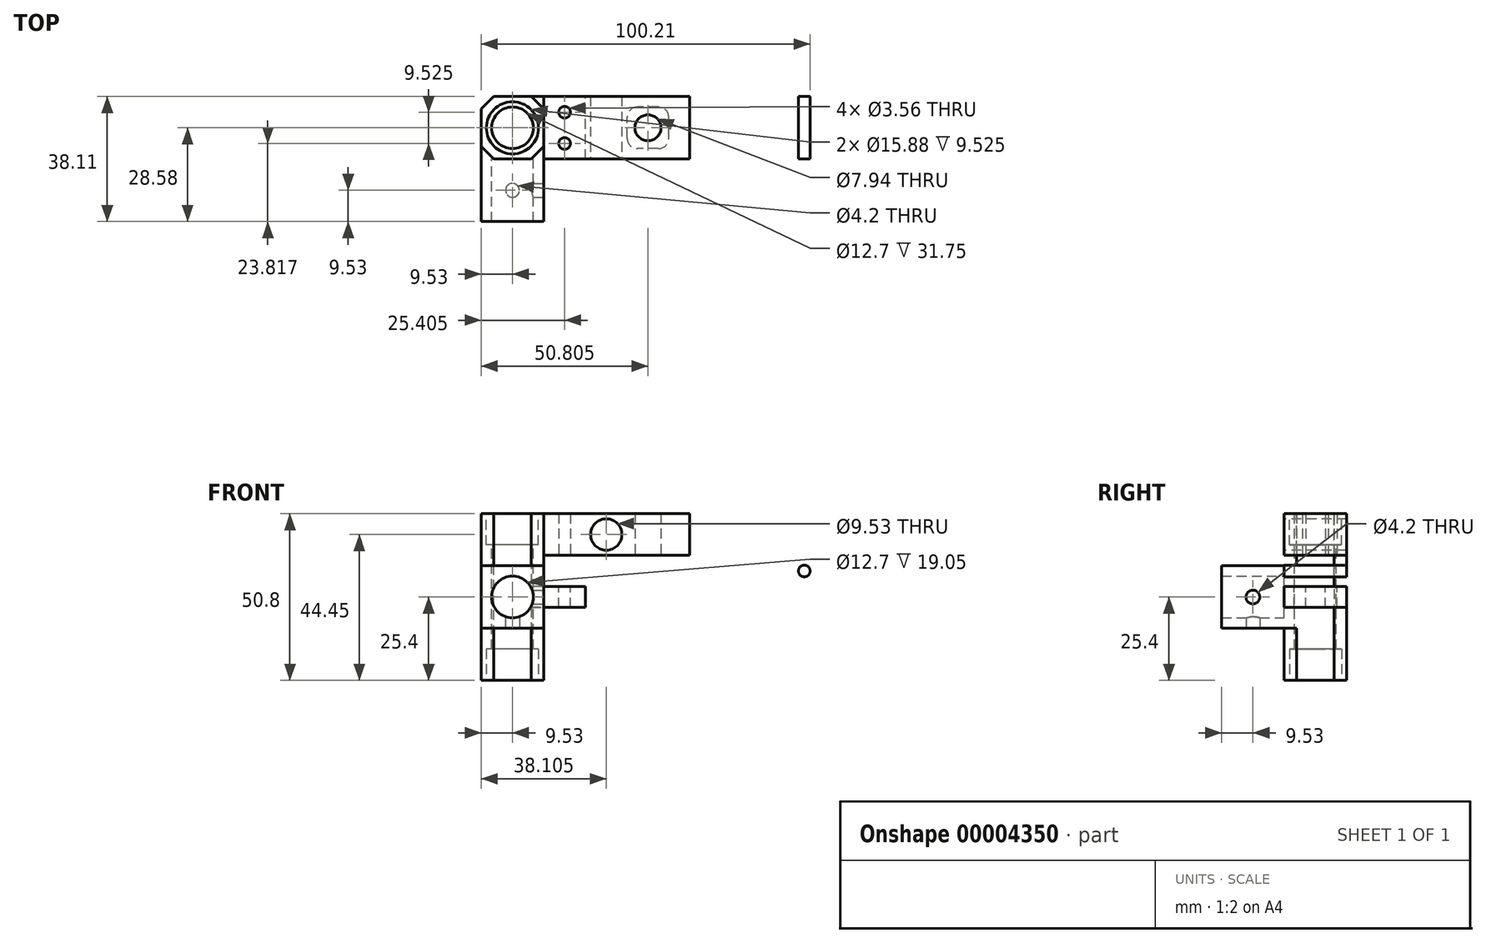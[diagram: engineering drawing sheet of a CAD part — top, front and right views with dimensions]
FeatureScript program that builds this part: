
annotation { "Feature Type Name" : "Feature", "Feature Type Description" : "" }
export const myFeature = defineFeature(function(context is Context, id is Id, definition is map)
    precondition{}
    {
        {
            var Q0;
            Q0=qCreatedBy(makeId("Front.planeOp"),FACE);
            var sketch = newSketch(context, id + "F0", { "sketchPlane" : qUnion([Q0])});
            skLineSegment(sketch, "E0.bottom", {"start": v(-9.52, -25.4) * mm, "end": v(9.53, -25.4) * mm});
            skLineSegment(sketch, "E0.top", {"start": v(-9.53, 0) * mm, "end": v(9.53, 0) * mm});
            skLineSegment(sketch, "E0.left", {"start": v(-9.52, -25.4) * mm, "end": v(-9.53, 0) * mm});
            skLineSegment(sketch, "E0.right", {"start": v(9.53, -25.4) * mm, "end": v(9.53, 0) * mm});
            skSolve(sketch);
        }
        {
            var Q0;
            Q0=makeQuery(id+"F0.imprint","IMPRINT",FACE,{"disambiguationData":[TD([[makeQuery(id+"F0.imprint","IMPRINT",EDGE,{"derivedFrom":sQuery(id+"F0.wireOp",EDGE,"E0.bottom")}),1.0]])]});
            extrude(context, id + "F1", {"entities" : qUnion([Q0]), "depth" : 19.05 * mm, "symmetric" : true});
        }
        {
            var Q0;
            Q0=makeQuery(id+"F1.opExtrude","SWEPT_FACE",FACE,{"disambiguationData":[OSD([sQuery(id+"F0.wireOp",EDGE,"E0.top")])]});
            var sketch = newSketch(context, id + "F2", { "sketchPlane" : qUnion([Q0])});
            skCircle(sketch, "E1", {"center": v(0, 0) * mm, "radius": 6.35 * mm});
            skCircle(sketch, "E2", {"center": v(0, 0) * mm, "radius": 7.94 * mm});
            skSolve(sketch);
        }
        {
            var Q0;
            Q0=makeQuery(id+"F2.imprint","IMPRINT",FACE,{"disambiguationData":[TD([[makeQuery(id+"F2.imprint","IMPRINT",EDGE,{"derivedFrom":sQuery(id+"F2.wireOp",EDGE,"E1")}),1.0]])]});
            extrude(context, id + "F3", {"entities" : qUnion([Q0]), "operationType" : NewBodyOperationType.REMOVE, "endBound" : BoundingType.UP_TO_NEXT, "oppositeDirection" : true, "depth" : 25.4 * mm});
        }
        {
            var Q0;
            Q0=makeQuery(id+"F2.imprint","IMPRINT",FACE,{"disambiguationData":[TD([[makeQuery(id+"F2.imprint","IMPRINT",EDGE,{"derivedFrom":sQuery(id+"F2.wireOp",EDGE,"E1")}),-1.0]])]});
            extrude(context, id + "F4", {"entities" : qUnion([Q0]), "operationType" : NewBodyOperationType.REMOVE, "oppositeDirection" : true, "depth" : 9.52 * mm});
        }
        {
            var Q0;
            Q0=makeQuery(id+"F1.opExtrude","SWEPT_BODY",BODY,{"disambiguationData":[OSD([sQuery(id+"F0.wireOp",EDGE,"E0.bottom"),sQuery(id+"F0.wireOp",EDGE,"E0.top"),sQuery(id+"F0.wireOp",EDGE,"E0.left"),sQuery(id+"F0.wireOp",EDGE,"E0.right")])]});
            var Q1;
            Q1=makeQuery(id+"F1.opExtrude","SWEPT_FACE",FACE,{"disambiguationData":[OSD([sQuery(id+"F0.wireOp",EDGE,"E0.bottom")])]});
            mirror(context, id + "F5", {"entities" : qUnion([Q0]), "mirrorPlane" : qUnion([Q1])});
        }
        {
            var Q0;
            Q0=makeQuery(id+"F1.opExtrude","SWEPT_BODY",BODY,{"disambiguationData":[OSD([sQuery(id+"F0.wireOp",EDGE,"E0.bottom"),sQuery(id+"F0.wireOp",EDGE,"E0.top"),sQuery(id+"F0.wireOp",EDGE,"E0.left"),sQuery(id+"F0.wireOp",EDGE,"E0.right")])]});
            var Q1;
            Q1=makeQuery(id+"F5.opPattern","COPY",BODY,{"derivedFrom":makeQuery(id+"F1.opExtrude","SWEPT_BODY",BODY,{"disambiguationData":[OSD([sQuery(id+"F0.wireOp",EDGE,"E0.bottom"),sQuery(id+"F0.wireOp",EDGE,"E0.top"),sQuery(id+"F0.wireOp",EDGE,"E0.left"),sQuery(id+"F0.wireOp",EDGE,"E0.right")])]}),"instanceName":"1"});
            booleanBodies(context, id + "F6", {"operationType" : BooleanOperationType.UNION, "tools" : qUnion([Q0, Q1])});
        }
        {
            var Q0;
            {var subQ0=makeQuery(id+"F1.opExtrude","CAP_FACE",FACE,{"disambiguationData":[OSD([sQuery(id+"F0.wireOp",EDGE,"E0.bottom"),sQuery(id+"F0.wireOp",EDGE,"E0.top"),sQuery(id+"F0.wireOp",EDGE,"E0.left"),sQuery(id+"F0.wireOp",EDGE,"E0.right")])],"isStart":false});Q0=makeQuery(id+"F6.opBoolean","MERGE",FACE,{"derivedFrom":[subQ0,makeQuery(id+"F5.opPattern","COPY",FACE,{"derivedFrom":subQ0,"instanceName":"1"})]});}
            var sketch = newSketch(context, id + "F7", { "sketchPlane" : qUnion([Q0])});
            skLineSegment(sketch, "E3.rect.bottom", {"start": v(9.53, -34.92) * mm, "end": v(-9.52, -34.92) * mm});
            skLineSegment(sketch, "E3.rect.top", {"start": v(9.53, -15.88) * mm, "end": v(-9.52, -15.88) * mm});
            skLineSegment(sketch, "E3.rect.left", {"start": v(9.53, -34.92) * mm, "end": v(9.53, -15.88) * mm});
            skLineSegment(sketch, "E3.rect.right", {"start": v(-9.52, -34.92) * mm, "end": v(-9.52, -15.88) * mm});
            skPoint(sketch, "E3.rect.middle", {"position": v(0, -25.4) * mm});
            skLineSegment(sketch, "E4", {"start": v(0, 0) * mm, "end": v(0, -50.8) * mm, "construction": true});
            skCircle(sketch, "E5", {"center": v(0, -25.4) * mm, "radius": 6.35 * mm});
            skLineSegment(sketch, "E6", {"start": v(0, -31.75) * mm, "end": v(0, -34.92) * mm, "construction": true});
            skSolve(sketch);
        }
        {
            var Q0;
            Q0 = qSketchRegion(id + "F7", true);
            extrude(context, id + "F8", {"entities" : qUnion([Q0]), "operationType" : NewBodyOperationType.ADD, "depth" : 19.05 * mm});
        }
        {
            var Q0;
            Q0=makeQuery(id+"F8.opExtrude","CAP_VERTEX",VERTEX,{"disambiguationData":[OSD([sQuery(id+"F7.wireOp",EDGE,"E3.rect.bottom"),sQuery(id+"F7.wireOp",EDGE,"E3.rect.left")])],"isStart":true});
            var Q1;
            Q1=makeQuery(id+"F8.opExtrude","CAP_VERTEX",VERTEX,{"disambiguationData":[OSD([sQuery(id+"F7.wireOp",EDGE,"E3.rect.bottom"),sQuery(id+"F7.wireOp",EDGE,"E3.rect.left")])],"isStart":false});
            var Q2;
            Q2=makeQuery(id+"F8.opExtrude","CAP_VERTEX",VERTEX,{"disambiguationData":[OSD([sQuery(id+"F7.wireOp",EDGE,"E3.rect.top"),sQuery(id+"F7.wireOp",EDGE,"E3.rect.right")])],"isStart":false});
            cPlane(context, id + "F9", {"entities" : qUnion([Q0, Q1, Q2]), "cplaneType" : CPlaneType.THREE_POINT, "offset" : 152.4 * mm, "width" : 152.4 * mm, "height" : 152.4 * mm});
        }
        {
            var Q0;
            Q0=makeQuery(id+"F8.opExtrude","SWEPT_FACE",FACE,{"disambiguationData":[OSD([sQuery(id+"F7.wireOp",EDGE,"E3.rect.left")])]});
            var sketch = newSketch(context, id + "F10", { "sketchPlane" : qUnion([Q0])});
            skCircle(sketch, "E7", {"center": v(-19.05, -25.4) * mm, "radius": 2.1 * mm});
            skLineSegment(sketch, "E8", {"start": v(-19.05, -15.88) * mm, "end": v(-19.05, -34.92) * mm, "construction": true});
            skLineSegment(sketch, "E9", {"start": v(-28.58, -25.4) * mm, "end": v(-15.88, -25.4) * mm, "construction": true});
            skSolve(sketch);
        }
        {
            var Q0;
            Q0=makeQuery(id+"F10.imprint","IMPRINT",FACE,{"disambiguationData":[TD([[makeQuery(id+"F10.imprint","IMPRINT",EDGE,{"derivedFrom":sQuery(id+"F10.wireOp",EDGE,"E7")}),1.0]])]});
            var Q1;
            Q1=sQuery(id+"F10.wireOp",EDGE,"E7");
            extrude(context, id + "F11", {"entities" : qUnion([Q0]), "operationType" : NewBodyOperationType.REMOVE, "surfaceEntities" : qUnion([Q1]), "endBound" : BoundingType.UP_TO_NEXT, "oppositeDirection" : true, "depth" : 25.4 * mm});
        }
        {
            var Q0;
            Q0=makeQuery(id+"F11.boolean.opBoolean","COPY",FACE,{"derivedFrom":makeQuery(id+"F11.opExtrude","SWEPT_FACE",FACE,{"disambiguationData":[OSD([sQuery(id+"F10.wireOp",EDGE,"E7")])]})});
            var Q1;
            Q1=qCreatedBy(id+"F9.planeOp",FACE);
            mirror(context, id + "F12", {"faces" : qUnion([Q0]), "mirrorPlane" : qUnion([Q1]), "patternType" : MirrorType.FACE});
        }
        {
            var Q0;
            {var subQ0=makeQuery(id+"F1.opExtrude","SWEPT_FACE",FACE,{"disambiguationData":[OSD([sQuery(id+"F0.wireOp",EDGE,"E0.right")])]});Q0=makeQuery(id+"F6.opBoolean","MERGE",FACE,{"derivedFrom":[subQ0,makeQuery(id+"F5.opPattern","COPY",FACE,{"derivedFrom":subQ0,"instanceName":"1"})]});}
            var sketch = newSketch(context, id + "F13", { "sketchPlane" : qUnion([Q0])});
            skLineSegment(sketch, "E10.bottom", {"start": v(-9.53, -22.22) * mm, "end": v(9.53, -22.22) * mm});
            skLineSegment(sketch, "E10.top", {"start": v(-9.53, -28.58) * mm, "end": v(9.53, -28.58) * mm});
            skLineSegment(sketch, "E10.left", {"start": v(-9.53, -22.22) * mm, "end": v(-9.53, -28.58) * mm});
            skLineSegment(sketch, "E10.right", {"start": v(9.53, -22.22) * mm, "end": v(9.53, -28.58) * mm});
            skPoint(sketch, "E11", {"position": v(-9.53, -25.4) * mm});
            skSolve(sketch);
        }
        {
            var Q0;
            Q0=makeQuery(id+"F13.imprint","IMPRINT",FACE,{"disambiguationData":[TD([[makeQuery(id+"F13.imprint","IMPRINT",EDGE,{"derivedFrom":sQuery(id+"F13.wireOp",EDGE,"E10.bottom")}),-1.0]])]});
            extrude(context, id + "F14", {"entities" : qUnion([Q0]), "operationType" : NewBodyOperationType.ADD, "depth" : 12.7 * mm});
        }
        {
            var Q0;
            {var subQ0=makeQuery(id+"F1.opExtrude","CAP_EDGE",EDGE,{"disambiguationData":[OSD([sQuery(id+"F0.wireOp",EDGE,"E0.left")])],"isStart":false});Q0=makeQuery(id+"F6.opBoolean","MERGE",EDGE,{"derivedFrom":[subQ0,makeQuery(id+"F5.opPattern","COPY",EDGE,{"derivedFrom":subQ0,"instanceName":"1"})]});}
            var Q1;
            {var subQ0=makeQuery(id+"F1.opExtrude","CAP_EDGE",EDGE,{"disambiguationData":[OSD([sQuery(id+"F0.wireOp",EDGE,"E0.left")])],"isStart":true});Q1=makeQuery(id+"F6.opBoolean","MERGE",EDGE,{"derivedFrom":[subQ0,makeQuery(id+"F5.opPattern","COPY",EDGE,{"derivedFrom":subQ0,"instanceName":"1"})]});}
            var Q2;
            {var subQ0=makeQuery(id+"F1.opExtrude","CAP_EDGE",EDGE,{"disambiguationData":[OSD([sQuery(id+"F0.wireOp",EDGE,"E0.right")])],"isStart":true});Q2=makeQuery(id+"F6.opBoolean","MERGE",EDGE,{"derivedFrom":[subQ0,makeQuery(id+"F5.opPattern","COPY",EDGE,{"derivedFrom":subQ0,"instanceName":"1"})]});}
            var Q3;
            {var subQ0=makeQuery(id+"F1.opExtrude","CAP_EDGE",EDGE,{"disambiguationData":[OSD([sQuery(id+"F0.wireOp",EDGE,"E0.right")])],"isStart":false});Q3=makeQuery(id+"F6.opBoolean","MERGE",EDGE,{"derivedFrom":[subQ0,makeQuery(id+"F5.opPattern","COPY",EDGE,{"derivedFrom":subQ0,"instanceName":"1"})]});}
            chamfer(context, id + "F15", {"entities" : qUnion([Q0, Q1, Q2, Q3]), "width" : 3.8 * mm, "tangentPropagation" : true});
        }
        {
            var Q0;
            Q0=makeQuery(id+"F14.opExtrude","SWEPT_FACE",FACE,{"disambiguationData":[OSD([sQuery(id+"F13.wireOp",EDGE,"E10.bottom")])]});
            var sketch = newSketch(context, id + "F16", { "sketchPlane" : qUnion([Q0])});
            skLineSegment(sketch, "E12", {"start": v(15.88, 9.53) * mm, "end": v(15.88, -9.53) * mm, "construction": true});
            skLineSegment(sketch, "E13", {"start": v(15.88, 0) * mm, "end": v(22.23, 0) * mm, "construction": true});
            skCircle(sketch, "E14", {"center": v(15.88, 4.76) * mm, "radius": 1.78 * mm});
            skCircle(sketch, "E15", {"center": v(15.88, -4.76) * mm, "radius": 1.78 * mm});
            skLineSegment(sketch, "E16", {"start": v(15.88, -4.76) * mm, "end": v(15.88, 4.76) * mm, "construction": true});
            skPoint(sketch, "E17", {"position": v(15.88, 0) * mm});
            skSolve(sketch);
        }
        {
            var Q0;
            Q0=makeQuery(id+"F16.imprint","IMPRINT",FACE,{"disambiguationData":[TD([[makeQuery(id+"F16.imprint","IMPRINT",EDGE,{"derivedFrom":sQuery(id+"F16.wireOp",EDGE,"E14")}),1.0]])]});
            var Q1;
            Q1=makeQuery(id+"F16.imprint","IMPRINT",FACE,{"disambiguationData":[TD([[makeQuery(id+"F16.imprint","IMPRINT",EDGE,{"derivedFrom":sQuery(id+"F16.wireOp",EDGE,"E15")}),1.0]])]});
            extrude(context, id + "F17", {"entities" : qUnion([Q0, Q1]), "operationType" : NewBodyOperationType.REMOVE, "endBound" : BoundingType.UP_TO_NEXT, "oppositeDirection" : true, "depth" : 25.4 * mm});
        }
        {
            var Q0;
            Q0=makeQuery(id+"F14.opExtrude","SWEPT_FACE",FACE,{"disambiguationData":[OSD([sQuery(id+"F13.wireOp",EDGE,"E10.bottom")])]});
            var sketch = newSketch(context, id + "F18", { "sketchPlane" : qUnion([Q0])});
            skLineSegment(sketch, "E18.bottom", {"start": v(9.53, -9.53) * mm, "end": v(76.2, -9.53) * mm});
            skLineSegment(sketch, "E18.top", {"start": v(9.52, 9.53) * mm, "end": v(76.2, 9.53) * mm});
            skLineSegment(sketch, "E18.left", {"start": v(9.53, -9.53) * mm, "end": v(9.52, 9.52) * mm});
            skLineSegment(sketch, "E18.right", {"start": v(76.2, -9.53) * mm, "end": v(76.2, 9.53) * mm});
            skPoint(sketch, "E19", {"position": v(0, 0) * mm});
            skPoint(sketch, "E20", {"position": v(9.53, 0) * mm});
            skSolve(sketch);
        }
        {
            var Q0;
            {var subQ1=sQuery(id+"F18.wireOp",EDGE,"E18.right");Q0=makeQuery(id+"F18.imprint","IMPRINT",FACE,{"disambiguationData":[TD([[makeQuery(id+"F18.imprint","IMPRINT",EDGE,{"derivedFrom":subQ1}),1.0]])]});}
            var Q1;
            {var subQ0=sQuery(id+"F13.wireOp",EDGE,"E10.bottom");var subQ1=makeQuery(id+"F14.opExtrude","CAP_EDGE",EDGE,{"disambiguationData":[OSD([subQ0])],"isStart":false});Q1=makeQuery(id+"F18.imprint","IMPRINT",FACE,{"disambiguationData":[TD([[makeQuery(id+"F18.imprint","IMPRINT",EDGE,{"derivedFrom":subQ1}),1.0]])]});}
            extrude(context, id + "F19", {"entities" : qUnion([Q0, Q1]), "depth" : 9.52 * mm});
        }
        {
            var Q0;
            Q0=makeQuery(id+"F19.opExtrude","CAP_FACE",FACE,{"disambiguationData":[OSD([sQuery(id+"F16.wireOp",EDGE,"E14"),sQuery(id+"F16.wireOp",EDGE,"E15"),sQuery(id+"F18.wireOp",EDGE,"E18.bottom"),sQuery(id+"F18.wireOp",EDGE,"E18.top"),sQuery(id+"F18.wireOp",EDGE,"E18.left"),sQuery(id+"F18.wireOp",EDGE,"E18.right")])],"isStart":false});
            var sketch = newSketch(context, id + "F20", { "sketchPlane" : qUnion([Q0])});
            skCircle(sketch, "E21", {"center": v(41.28, 0) * mm, "radius": 3.97 * mm});
            skLineSegment(sketch, "E22.rect.bottom", {"start": v(44.45, -6.35) * mm, "end": v(38.1, -6.35) * mm});
            skLineSegment(sketch, "E22.rect.top", {"start": v(44.45, 6.35) * mm, "end": v(38.1, 6.35) * mm});
            skLineSegment(sketch, "E22.rect.left", {"start": v(47.63, -3.18) * mm, "end": v(47.63, 3.17) * mm});
            skLineSegment(sketch, "E22.rect.right", {"start": v(34.93, -3.18) * mm, "end": v(34.93, 3.17) * mm});
            skPoint(sketch, "E23", {"position": v(22.23, 0) * mm});
            skPoint(sketch, "E24.visualSharp", {"position": v(47.63, 6.35) * mm});
            skArc(sketch, "E24.filletArc", {"start": v(47.63, 3.17) * mm, "mid": v(46.7, 5.42) * mm, "end": v(44.45, 6.35) * mm});
            skPoint(sketch, "E25.visualSharp", {"position": v(34.93, 6.35) * mm});
            skArc(sketch, "E25.filletArc", {"start": v(38.1, 6.35) * mm, "mid": v(35.85, 5.42) * mm, "end": v(34.93, 3.17) * mm});
            skPoint(sketch, "E26.visualSharp", {"position": v(34.93, -6.35) * mm});
            skArc(sketch, "E26.filletArc", {"start": v(34.93, -3.18) * mm, "mid": v(35.85, -5.42) * mm, "end": v(38.1, -6.35) * mm});
            skPoint(sketch, "E27.visualSharp", {"position": v(47.63, -6.35) * mm});
            skArc(sketch, "E27.filletArc", {"start": v(44.45, -6.35) * mm, "mid": v(46.7, -5.42) * mm, "end": v(47.63, -3.18) * mm});
            skLineSegment(sketch, "E28", {"start": v(41.28, 0) * mm, "end": v(0, 0) * mm, "construction": true});
            skLineSegment(sketch, "E29.bottom", {"start": v(9.53, 9.53) * mm, "end": v(53.98, 9.53) * mm});
            skLineSegment(sketch, "E29.top", {"start": v(9.53, -9.53) * mm, "end": v(53.98, -9.53) * mm});
            skLineSegment(sketch, "E29.left", {"start": v(9.53, 9.53) * mm, "end": v(9.53, -9.53) * mm});
            skLineSegment(sketch, "E29.right", {"start": v(53.98, 9.53) * mm, "end": v(53.98, -9.53) * mm});
            skSolve(sketch);
        }
        {
            var Q0;
            Q0=makeQuery(id+"F20.imprint","IMPRINT",FACE,{"disambiguationData":[TD([[makeQuery(id+"F20.imprint","IMPRINT",EDGE,{"derivedFrom":sQuery(id+"F20.wireOp",EDGE,"E22.rect.bottom")}),1.0]])]});
            var Q1;
            Q1=makeQuery(id+"F20.imprint","IMPRINT",FACE,{"disambiguationData":[TD([[makeQuery(id+"F20.imprint","IMPRINT",EDGE,{"derivedFrom":sQuery(id+"F20.wireOp",EDGE,"E21")}),-1.0]])]});
            var Q2;
            Q2=qCreatedBy(makeId("Top.planeOp"),FACE);
            extrude(context, id + "F21", {"entities" : qUnion([Q0, Q1]), "endBound" : BoundingType.UP_TO_SURFACE, "endBoundEntityFace" : qUnion([Q2]), "depth" : 5 / 406.4 * mm});
        }
        {
            var Q0;
            Q0=makeQuery(id+"F20.imprint","IMPRINT",FACE,{"disambiguationData":[TD([[makeQuery(id+"F20.imprint","IMPRINT",EDGE,{"derivedFrom":sQuery(id+"F20.wireOp",EDGE,"E21")}),-1.0]])]});
            extrude(context, id + "F22", {"entities" : qUnion([Q0]), "operationType" : NewBodyOperationType.REMOVE, "depth" : 1 / 101.6 * mm});
        }
        {
            var Q0;
            Q0=makeQuery(id+"F20.imprint","IMPRINT",FACE,{"disambiguationData":[TD([[makeQuery(id+"F20.imprint","IMPRINT",EDGE,{"derivedFrom":sQuery(id+"F20.wireOp",EDGE,"E21")}),1.0]])]});
            extrude(context, id + "F23", {"entities" : qUnion([Q0]), "operationType" : NewBodyOperationType.REMOVE, "endBound" : BoundingType.UP_TO_NEXT, "oppositeDirection" : true, "depth" : 3 / 406.4 * mm});
        }
        {
            var Q0;
            Q0=makeQuery(id+"F19.opExtrude","SWEPT_BODY",BODY,{"disambiguationData":[OSD([sQuery(id+"F16.wireOp",EDGE,"E14"),sQuery(id+"F16.wireOp",EDGE,"E15"),sQuery(id+"F18.wireOp",EDGE,"E18.bottom"),sQuery(id+"F18.wireOp",EDGE,"E18.top"),sQuery(id+"F18.wireOp",EDGE,"E18.left"),sQuery(id+"F18.wireOp",EDGE,"E18.right")])]});
            var Q1;
            Q1=makeQuery(id+"F19.opExtrude","SWEPT_FACE",FACE,{"disambiguationData":[OSD([sQuery(id+"F18.wireOp",EDGE,"E18.right")])]});
            mirror(context, id + "F24", {"entities" : qUnion([Q0]), "mirrorPlane" : qUnion([Q1])});
        }
        {
            var Q0;
            Q0=makeQuery(id+"F19.opExtrude","SWEPT_BODY",BODY,{"disambiguationData":[OSD([sQuery(id+"F16.wireOp",EDGE,"E14"),sQuery(id+"F16.wireOp",EDGE,"E15"),sQuery(id+"F18.wireOp",EDGE,"E18.bottom"),sQuery(id+"F18.wireOp",EDGE,"E18.top"),sQuery(id+"F18.wireOp",EDGE,"E18.left"),sQuery(id+"F18.wireOp",EDGE,"E18.right")])]});
            var Q1;
            Q1=makeQuery(id+"F24.opPattern","COPY",BODY,{"derivedFrom":makeQuery(id+"F19.opExtrude","SWEPT_BODY",BODY,{"disambiguationData":[OSD([sQuery(id+"F16.wireOp",EDGE,"E14"),sQuery(id+"F16.wireOp",EDGE,"E15"),sQuery(id+"F18.wireOp",EDGE,"E18.bottom"),sQuery(id+"F18.wireOp",EDGE,"E18.top"),sQuery(id+"F18.wireOp",EDGE,"E18.left"),sQuery(id+"F18.wireOp",EDGE,"E18.right")])]}),"instanceName":"1"});
            booleanBodies(context, id + "F25", {"operationType" : BooleanOperationType.UNION, "tools" : qUnion([Q0, Q1])});
        }
        {
            var Q0;
            Q0=makeQuery(id+"F21.opExtrude","SWEPT_FACE",FACE,{"disambiguationData":[OSD([sQuery(id+"F20.wireOp",EDGE,"E29.top")])]});
            var sketch = newSketch(context, id + "F26", { "sketchPlane" : qUnion([Q0])});
            skCircle(sketch, "E30", {"center": v(28.58, -6.35) * mm, "radius": 4.76 * mm});
            skLineSegment(sketch, "E31", {"start": v(28.58, -6.35) * mm, "end": v(28.58, -12.7) * mm, "construction": true});
            skPoint(sketch, "E32", {"position": v(22.23, -12.7) * mm});
            skPoint(sketch, "E33", {"position": v(34.93, -12.7) * mm});
            skLineSegment(sketch, "E34", {"start": v(22.23, -12.7) * mm, "end": v(34.93, -12.7) * mm, "construction": true});
            skLineSegment(sketch, "E35", {"start": v(28.58, -6.35) * mm, "end": v(28.58, 0) * mm, "construction": true});
            skSolve(sketch);
        }
        {
            var Q0;
            Q0=makeQuery(id+"F26.imprint","IMPRINT",FACE,{"disambiguationData":[TD([[makeQuery(id+"F26.imprint","IMPRINT",EDGE,{"derivedFrom":sQuery(id+"F26.wireOp",EDGE,"E30")}),1.0]])]});
            extrude(context, id + "F27", {"entities" : qUnion([Q0]), "operationType" : NewBodyOperationType.REMOVE, "endBound" : BoundingType.UP_TO_NEXT, "oppositeDirection" : true, "depth" : 25.4 * mm});
        }
        {
            var Q0;
            {var subQ0=makeQuery(id+"F19.opExtrude","SWEPT_FACE",FACE,{"disambiguationData":[OSD([sQuery(id+"F18.wireOp",EDGE,"E18.bottom")])]});Q0=makeQuery(id+"F25.opBoolean","MERGE",FACE,{"derivedFrom":[subQ0,makeQuery(id+"F24.opPattern","COPY",FACE,{"derivedFrom":subQ0,"instanceName":"1"})]});}
            var sketch = newSketch(context, id + "F29", { "sketchPlane" : qUnion([Q0])});
            skCircle(sketch, "E36", {"center": v(63.5, -17.46) * mm, "radius": 1.78 * mm});
            skLineSegment(sketch, "E37", {"start": v(76.2, -12.7) * mm, "end": v(76.2, -22.22) * mm, "construction": true});
            skLineSegment(sketch, "E38", {"start": v(76.2, -17.46) * mm, "end": v(63.5, -17.46) * mm, "construction": true});
            skCircle(sketch, "E39.0.MirrorC", {"center": v(88.9, -17.46) * mm, "radius": 1.78 * mm});
            skSolve(sketch);
        }
        {
            var Q0;
            Q0=makeQuery(id+"F29.imprint","IMPRINT",FACE,{"disambiguationData":[TD([[makeQuery(id+"F29.imprint","IMPRINT",EDGE,{"derivedFrom":sQuery(id+"F29.wireOp",EDGE,"E36")}),1.0]])]});
            var Q1;
            Q1=makeQuery(id+"F29.imprint","IMPRINT",FACE,{"disambiguationData":[TD([[makeQuery(id+"F29.imprint","IMPRINT",EDGE,{"derivedFrom":sQuery(id+"F29.wireOp",EDGE,"E39.0.MirrorC")}),-1.0]])]});
            extrude(context, id + "F28", {"entities" : qUnion([Q0, Q1]), "operationType" : NewBodyOperationType.REMOVE, "endBound" : BoundingType.UP_TO_NEXT, "oppositeDirection" : true, "depth" : 25.4 * mm});
        }
    });
